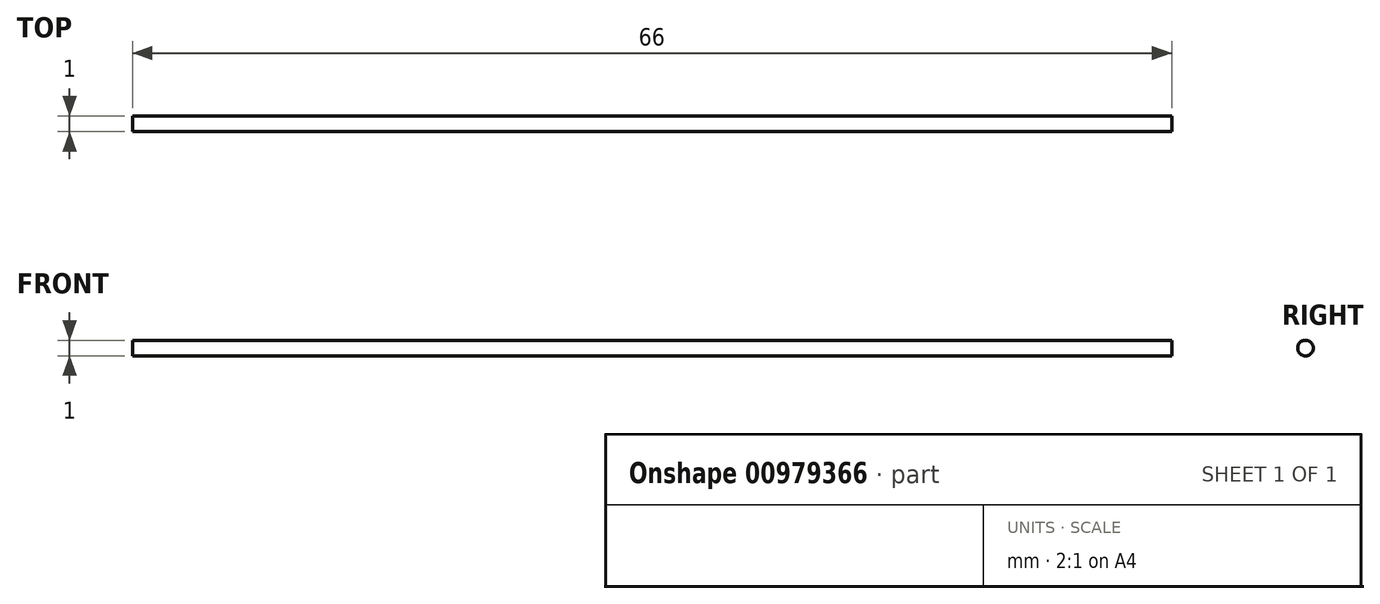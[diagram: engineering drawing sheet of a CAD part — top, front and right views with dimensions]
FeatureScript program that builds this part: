
annotation { "Feature Type Name" : "Feature", "Feature Type Description" : "" }
export const myFeature = defineFeature(function(context is Context, id is Id, definition is map)
    precondition{}
    {
        {
            var Q0;
            Q0=qCreatedBy(makeId("Front.planeOp"),FACE);
            var sketch = newSketch(context, id + "F0", { "sketchPlane" : qUnion([Q0])});
            skLineSegment(sketch, "E0", {"start": v(-32.81, 0) * mm, "end": v(33.19, 0) * mm});
            skSolve(sketch);
        }
        {
            var Q0;
            Q0=qCreatedBy(makeId("Right.planeOp"),FACE);
            var sketch = newSketch(context, id + "F1", { "sketchPlane" : qUnion([Q0])});
            skCircle(sketch, "E1", {"center": v(0, 0) * mm, "radius": 0.5 * mm});
            skSolve(sketch);
        }
        {
            var Q0;
            Q0=makeQuery(id+"F1.imprint","IMPRINT",FACE,{"disambiguationData":[TD([[makeQuery(id+"F1.imprint","IMPRINT",EDGE,{"derivedFrom":sQuery(id+"F1.wireOp",EDGE,"E1")}),1.0]])]});
            var Q1;
            Q1=sQuery(id+"F0.wireOp",EDGE,"E0");
            sweep(context, id + "F2", {"profiles" : qUnion([Q0]), "path" : qUnion([Q1])});
        }
    });
